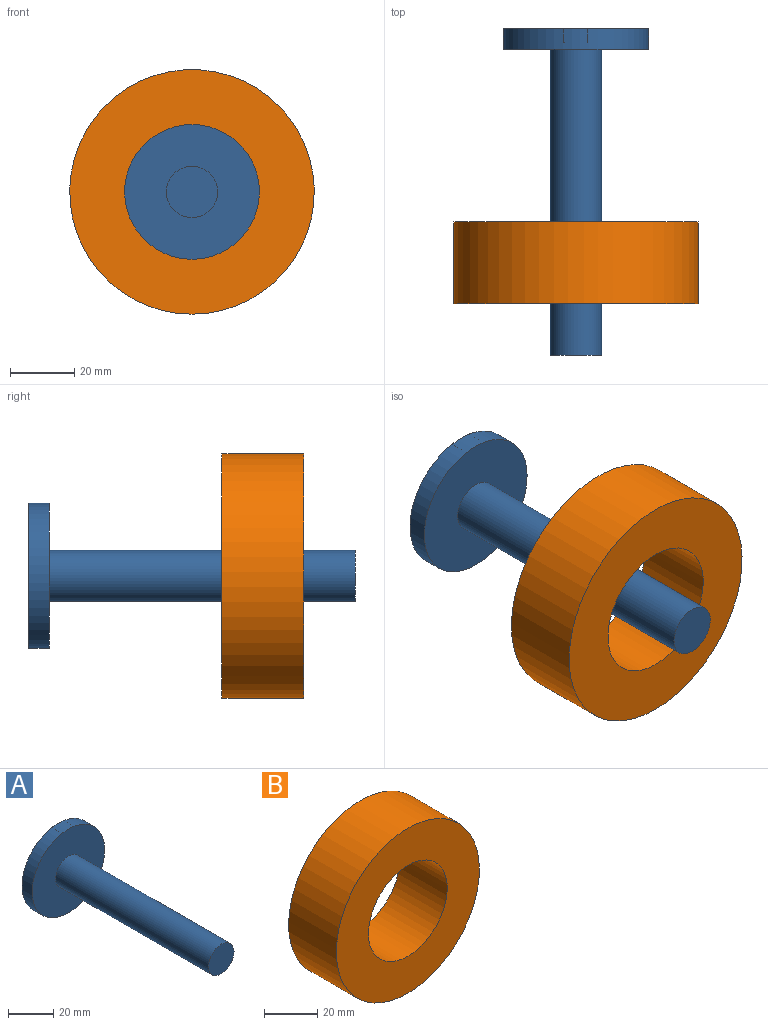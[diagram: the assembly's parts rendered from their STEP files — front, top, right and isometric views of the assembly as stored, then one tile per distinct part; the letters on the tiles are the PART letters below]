
ASSEMBLY  parts=2 mates=1
PART A: 10 faces, bbox 45.2x101.6x45.2 mm
  f0: cylinder r=22.6mm len=45.21mm, axis (0,1,0), area 901.9mm2, adj f1,f2
  f1: plane 45.21x45.21mm, normal (0,-1,0), area 1405.2mm2, adj f0,f3
  f2: plane 45.21x45.21mm, normal (0,1,0), area 1277.8mm2, adj f0,f5,f6,f7,f8
  f3: cylinder r=7.98mm len=95.25mm, axis (0,1,0), area 4774.9mm2, adj f1,f4
  f4: plane 15.96x15.96mm, normal (0,-1,0), area 200mm2, adj f3
  f5: plane 43.75x4.32mm, normal (-1,0,0), area 188.9mm2, adj f2,f6,f8,f9
  f6: plane 7.48x4.32mm, normal (0,0,-1), area 32.3mm2, adj f2,f5,f7,f9
  f7: plane 43.75x4.32mm, normal (1,0,0), area 188.9mm2, adj f2,f6,f8,f9
  f8: plane 7.48x4.32mm, normal (0,0,1), area 32.3mm2, adj f2,f5,f7,f9
  f9: plane 43.75x7.48mm, normal (0,1,0), area 327.4mm2, adj f5,f6,f7,f8
PART B: 4 faces, bbox 76.1x25.4x76.1 mm
  f0: cylinder r=38.06mm len=76.12mm, axis (0,1,0), area 6073.9mm2, adj f1,f2
  f1: plane 76.12x76.12mm, normal (0,-1,0), area 3170.1mm2, adj f0,f3
  f2: plane 76.12x76.12mm, normal (0,1,0), area 3170.1mm2, adj f0,f3
  f3: cylinder r=20.96mm len=41.92mm, axis (0,1,0), area 3345.3mm2, adj f1,f2
PLACE A t=(1.45,-23.03,34.57)mm
PLACE B t=(1.45,-83.16,34.57)mm
MATE cylindrical A.f3 <-> B.f3  axis (0,-1,0) through (1.45,-124.63,34.57)mm
